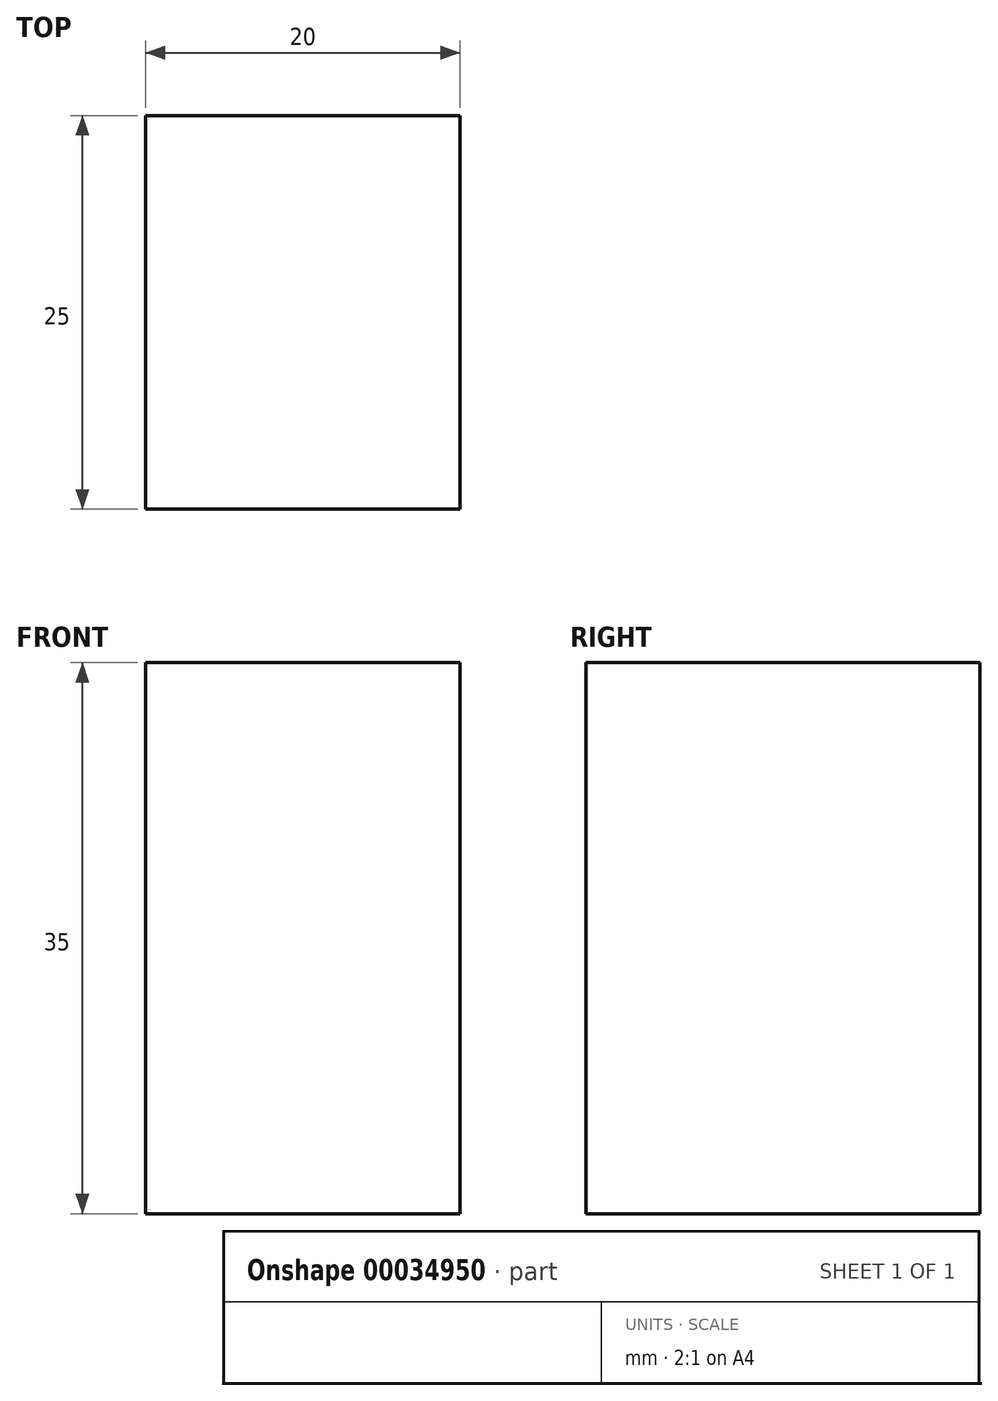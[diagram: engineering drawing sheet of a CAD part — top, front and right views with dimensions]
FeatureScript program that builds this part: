
annotation { "Feature Type Name" : "Feature", "Feature Type Description" : "" }
export const myFeature = defineFeature(function(context is Context, id is Id, definition is map)
    precondition{}
    {
        {
            var Q0;
            Q0=qCreatedBy(makeId("Front.planeOp"),FACE);
            var sketch = newSketch(context, id + "F0", { "sketchPlane" : qUnion([Q0])});
            skLineSegment(sketch, "E0.rect.bottom", {"start": v(10, 17.5) * mm, "end": v(-10, 17.5) * mm});
            skLineSegment(sketch, "E0.rect.top", {"start": v(10, -17.5) * mm, "end": v(-10, -17.5) * mm});
            skLineSegment(sketch, "E0.rect.left", {"start": v(10, 17.5) * mm, "end": v(10, -17.5) * mm});
            skLineSegment(sketch, "E0.rect.right", {"start": v(-10, 17.5) * mm, "end": v(-10, -17.5) * mm});
            skPoint(sketch, "E0.rect.middle", {"position": v(0, 0) * mm});
            skSolve(sketch);
        }
        {
            var Q0;
            Q0=makeQuery(id+"F0.imprint","IMPRINT",FACE,{"disambiguationData":[TD([[makeQuery(id+"F0.imprint","IMPRINT",EDGE,{"derivedFrom":sQuery(id+"F0.wireOp",EDGE,"E0.rect.bottom")}),1.0]])]});
            extrude(context, id + "F1", {"entities" : qUnion([Q0]), "depth" : 25 * mm});
        }
    });
